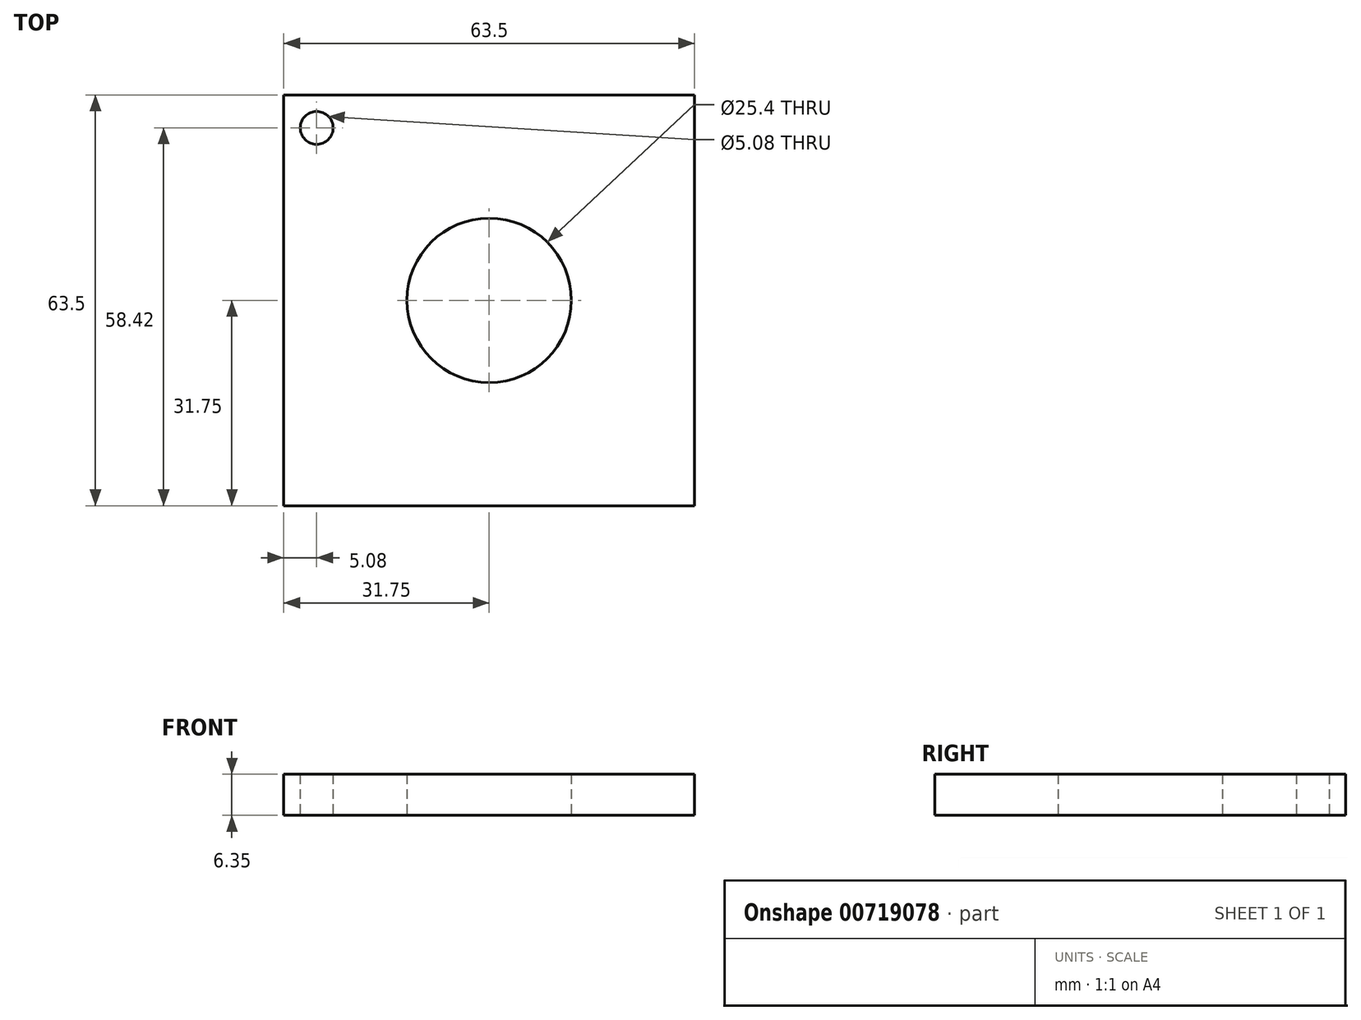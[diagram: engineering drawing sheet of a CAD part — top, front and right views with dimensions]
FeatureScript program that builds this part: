
annotation { "Feature Type Name" : "Feature", "Feature Type Description" : "" }
export const myFeature = defineFeature(function(context is Context, id is Id, definition is map)
    precondition{}
    {
        {
            var Q0;
            Q0=qCreatedBy(makeId("Top.planeOp"),FACE);
            var sketch = newSketch(context, id + "F0", { "sketchPlane" : qUnion([Q0])});
            skLineSegment(sketch, "E0.bottom", {"start": v(31.75, -31.75) * mm, "end": v(-31.75, -31.75) * mm});
            skLineSegment(sketch, "E0.top", {"start": v(31.75, 31.75) * mm, "end": v(-31.75, 31.75) * mm});
            skLineSegment(sketch, "E0.left", {"start": v(31.75, -31.75) * mm, "end": v(31.75, 31.75) * mm});
            skLineSegment(sketch, "E0.right", {"start": v(-31.75, -31.75) * mm, "end": v(-31.75, 31.75) * mm});
            skPoint(sketch, "E0.middle", {"position": v(0, 0) * mm});
            skSolve(sketch);
        }
        {
            var Q0;
            Q0=makeQuery(id+"F0.imprint","IMPRINT",FACE,{"disambiguationData":[TD([[makeQuery(id+"F0.imprint","IMPRINT",EDGE,{"derivedFrom":sQuery(id+"F0.wireOp",EDGE,"E0.bottom")}),-1.0]])]});
            extrude(context, id + "F1", {"entities" : qUnion([Q0]), "depth" : 6.35 * mm, "offsetDistance" : 25.4 * mm});
        }
        {
            var Q0;
            Q0=qCreatedBy(makeId("Top.planeOp"),FACE);
            var sketch = newSketch(context, id + "F2", { "sketchPlane" : qUnion([Q0])});
            skCircle(sketch, "E1", {"center": v(0, 0) * mm, "radius": 12.7 * mm});
            skSolve(sketch);
        }
        {
            var Q0;
            Q0 = qSketchRegion(id + "F2", true);
            extrude(context, id + "F3", {"entities" : qUnion([Q0]), "operationType" : NewBodyOperationType.REMOVE, "endBound" : BoundingType.UP_TO_NEXT, "depth" : 25.4 * mm, "offsetDistance" : 25.4 * mm});
        }
        {
            var Q0;
            Q0=qCreatedBy(makeId("Top.planeOp"),FACE);
            var sketch = newSketch(context, id + "F4", { "sketchPlane" : qUnion([Q0])});
            skCircle(sketch, "E2", {"center": v(-26.67, 26.67) * mm, "radius": 2.54 * mm});
            skSolve(sketch);
        }
        {
            var Q0;
            Q0 = qSketchRegion(id + "F4", true);
            extrude(context, id + "F5", {"entities" : qUnion([Q0]), "operationType" : NewBodyOperationType.REMOVE, "endBound" : BoundingType.UP_TO_NEXT, "depth" : 25.4 * mm, "offsetDistance" : 25.4 * mm});
        }
    });
